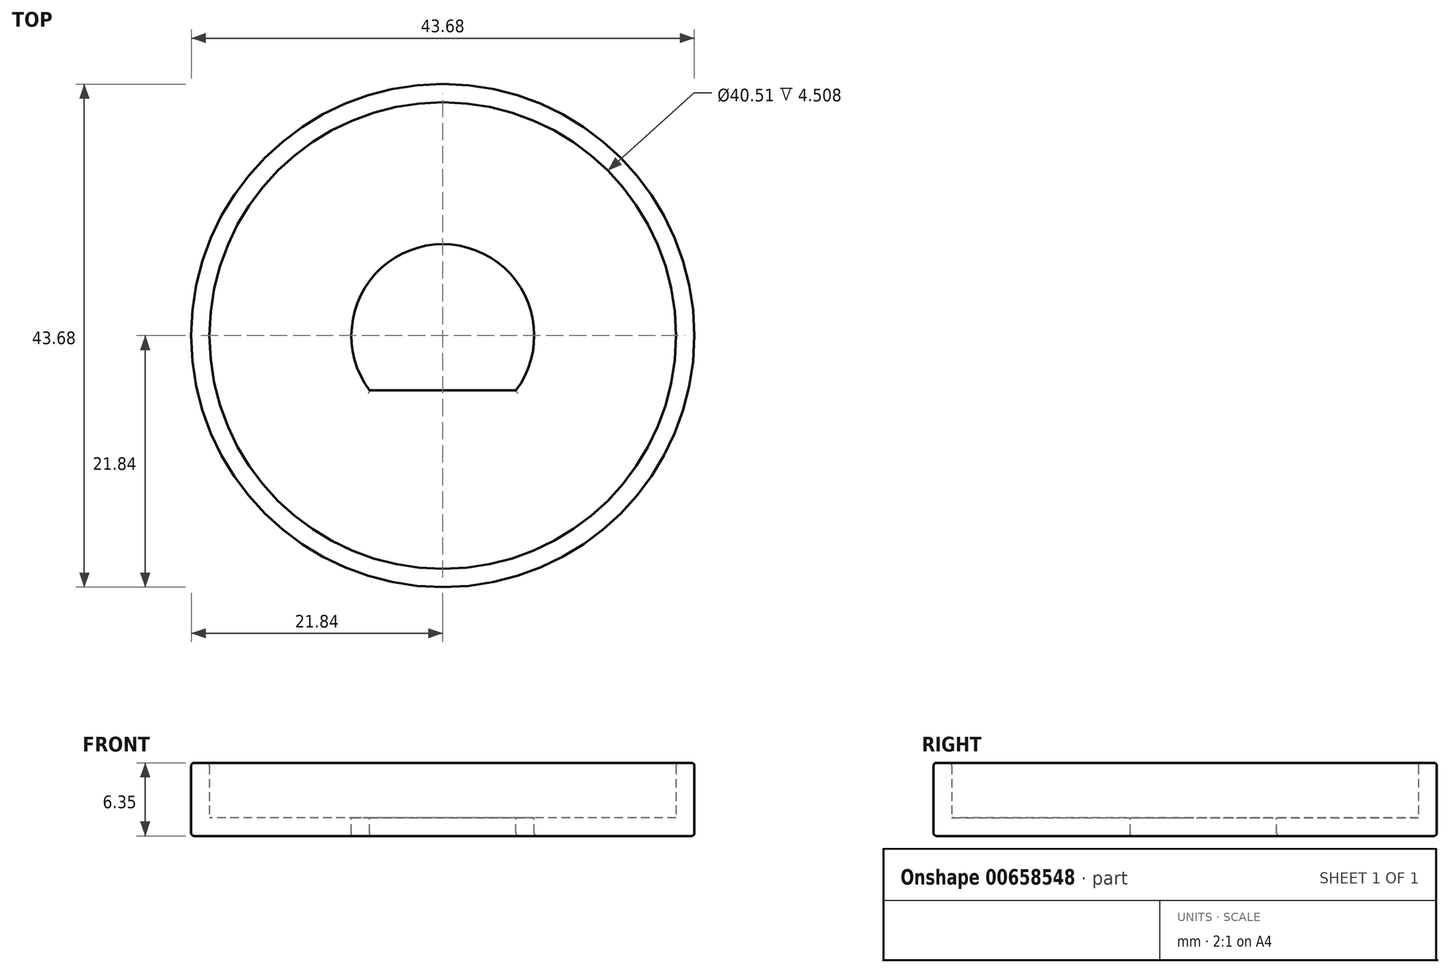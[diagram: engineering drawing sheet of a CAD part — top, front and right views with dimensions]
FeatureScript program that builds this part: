
annotation { "Feature Type Name" : "Feature", "Feature Type Description" : "" }
export const myFeature = defineFeature(function(context is Context, id is Id, definition is map)
    precondition{}
    {
        {
            var Q0;
            Q0=qCreatedBy(makeId("Top.planeOp"),FACE);
            var sketch = newSketch(context, id + "F0", { "sketchPlane" : qUnion([Q0])});
            skCircle(sketch, "E0", {"center": v(0, 0) * mm, "radius": 21.84 * mm});
            skSolve(sketch);
        }
        {
            var Q0;
            Q0 = qSketchRegion(id + "F0", true);
            extrude(context, id + "F1", {"entities" : qUnion([Q0]), "depth" : 1.59 * mm, "offsetDistance" : 25.4 * mm});
        }
        {
            var Q0;
            Q0=makeQuery(id+"F1.opExtrude","CAP_FACE",FACE,{"disambiguationData":[OSD([sQuery(id+"F0.wireOp",EDGE,"E0")])],"isStart":false});
            var sketch = newSketch(context, id + "F2", { "sketchPlane" : qUnion([Q0])});
            skCircle(sketch, "E1", {"center": v(0, 0) * mm, "radius": 21.84 * mm});
            skCircle(sketch, "E2", {"center": v(0, 0) * mm, "radius": 20.26 * mm});
            skSolve(sketch);
        }
        {
            var Q0;
            Q0 = qSketchRegion(id + "F2", true);
            extrude(context, id + "F3", {"entities" : qUnion([Q0]), "operationType" : NewBodyOperationType.ADD, "depth" : 4.76 * mm, "offsetDistance" : 25.4 * mm});
        }
        {
            var Q0;
            Q0=makeQuery(id+"F1.opExtrude","CAP_FACE",FACE,{"disambiguationData":[OSD([sQuery(id+"F0.wireOp",EDGE,"E0")])],"isStart":false});
            var sketch = newSketch(context, id + "F4", { "sketchPlane" : qUnion([Q0])});
            skArc(sketch, "E3", {"start": v(6.35, -4.76) * mm, "mid": v(0, 7.94) * mm, "end": v(-6.35, -4.76) * mm});
            skLineSegment(sketch, "E4", {"start": v(-6.35, -4.76) * mm, "end": v(6.35, -4.76) * mm});
            skSolve(sketch);
        }
        {
            var Q0;
            Q0 = qSketchRegion(id + "F4", true);
            extrude(context, id + "F5", {"entities" : qUnion([Q0]), "operationType" : NewBodyOperationType.REMOVE, "oppositeDirection" : true, "depth" : 25.4 * mm, "offsetDistance" : 25.4 * mm});
        }
        {
            var Q0;
            Q0=makeQuery(id+"F3.opExtrude","CAP_EDGE",EDGE,{"disambiguationData":[OSD([sQuery(id+"F2.wireOp",EDGE,"E1")])],"isStart":false});
            var Q1;
            Q1=makeQuery(id+"F3.opExtrude","CAP_EDGE",EDGE,{"disambiguationData":[OSD([sQuery(id+"F2.wireOp",EDGE,"E2")])],"isStart":false});
            var Q2;
            Q2=makeQuery(id+"F1.opExtrude","CAP_EDGE",EDGE,{"disambiguationData":[OSD([sQuery(id+"F0.wireOp",EDGE,"E0")])],"isStart":true});
            var Q3;
            Q3=makeQuery(id+"F5.boolean.opBoolean","COPY",EDGE,{"derivedFrom":makeQuery(id+"F5.opExtrude","CAP_EDGE",EDGE,{"disambiguationData":[OSD([sQuery(id+"F4.wireOp",EDGE,"E3")])],"isStart":true})});
            var Q4;
            Q4=makeQuery(id+"F5.boolean.opBoolean","INTERSECT",EDGE,{"derivedFrom":[makeQuery(id+"F1.opExtrude","CAP_FACE",FACE,{"disambiguationData":[OSD([sQuery(id+"F0.wireOp",EDGE,"E0")])],"isStart":true}),makeQuery(id+"F5.opExtrude","SWEPT_FACE",FACE,{"disambiguationData":[OSD([sQuery(id+"F4.wireOp",EDGE,"E3")])]})]});
            var Q5;
            Q5=makeQuery(id+"F5.boolean.opBoolean","COPY",EDGE,{"derivedFrom":makeQuery(id+"F5.opExtrude","CAP_EDGE",EDGE,{"disambiguationData":[OSD([sQuery(id+"F4.wireOp",EDGE,"E4")])],"isStart":true})});
            var Q6;
            Q6=makeQuery(id+"F5.boolean.opBoolean","INTERSECT",EDGE,{"derivedFrom":[makeQuery(id+"F1.opExtrude","CAP_FACE",FACE,{"disambiguationData":[OSD([sQuery(id+"F0.wireOp",EDGE,"E0")])],"isStart":true}),makeQuery(id+"F5.opExtrude","SWEPT_FACE",FACE,{"disambiguationData":[OSD([sQuery(id+"F4.wireOp",EDGE,"E4")])]})]});
            fillet(context, id + "F6", {"entities" : qUnion([Q0, Q1, Q2, Q3, Q4, Q5, Q6]), "radius" : 0.25 * mm, "tangentPropagation" : true, "allowEdgeOverflow" : false});
        }
    });
